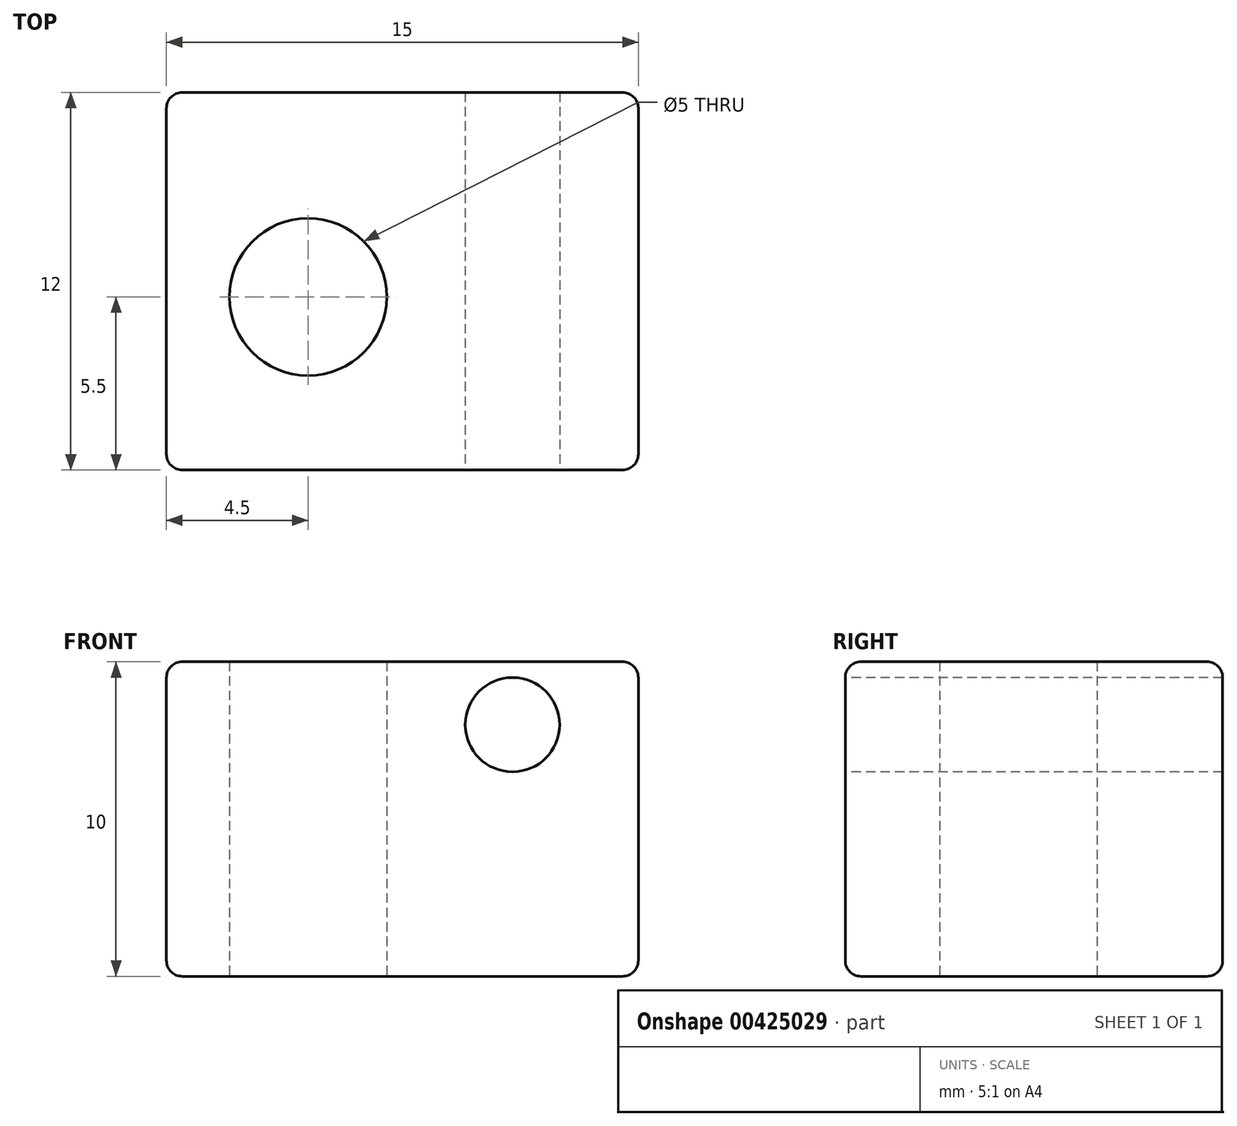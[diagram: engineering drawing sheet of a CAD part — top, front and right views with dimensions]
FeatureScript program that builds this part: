
annotation { "Feature Type Name" : "Feature", "Feature Type Description" : "" }
export const myFeature = defineFeature(function(context is Context, id is Id, definition is map)
    precondition{}
    {
        {
            var Q0;
            Q0=qCreatedBy(makeId("Top.planeOp"),FACE);
            var sketch = newSketch(context, id + "F0", { "sketchPlane" : qUnion([Q0])});
            skLineSegment(sketch, "E0.bottom", {"start": v(0, 0) * mm, "end": v(15, 0) * mm});
            skLineSegment(sketch, "E0.top", {"start": v(0, 12) * mm, "end": v(15, 12) * mm});
            skLineSegment(sketch, "E0.left", {"start": v(0, 0) * mm, "end": v(0, 12) * mm});
            skLineSegment(sketch, "E0.right", {"start": v(15, 0) * mm, "end": v(15, 12) * mm});
            skCircle(sketch, "E1", {"center": v(4.5, 5.5) * mm, "radius": 2.5 * mm});
            skSolve(sketch);
        }
        {
            var Q0;
            Q0=makeQuery(id+"F0.imprint","IMPRINT",FACE,{"disambiguationData":[TD([[makeQuery(id+"F0.imprint","IMPRINT",EDGE,{"derivedFrom":sQuery(id+"F0.wireOp",EDGE,"E0.bottom")}),1.0]])]});
            extrude(context, id + "F1", {"entities" : qUnion([Q0]), "endBound" : BoundingType.SYMMETRIC, "depth" : 10 * mm});
        }
        {
            var Q0;
            Q0=makeQuery(id+"F1.opExtrude","SWEPT_FACE",FACE,{"disambiguationData":[OSD([sQuery(id+"F0.wireOp",EDGE,"E0.bottom")])]});
            var sketch = newSketch(context, id + "F2", { "sketchPlane" : qUnion([Q0])});
            skCircle(sketch, "E2", {"center": v(11, 3) * mm, "radius": 1.5 * mm});
            skSolve(sketch);
        }
        {
            var Q0;
            Q0=makeQuery(id+"F2.imprint","IMPRINT",FACE,{"disambiguationData":[TD([[makeQuery(id+"F2.imprint","IMPRINT",EDGE,{"derivedFrom":sQuery(id+"F2.wireOp",EDGE,"E2")}),1.0]])]});
            extrude(context, id + "F3", {"entities" : qUnion([Q0]), "operationType" : NewBodyOperationType.REMOVE, "endBound" : BoundingType.THROUGH_ALL, "oppositeDirection" : true, "depth" : 25 * mm});
        }
        {
            var Q0;
            Q0=makeQuery(id+"F1.opExtrude","CAP_EDGE",EDGE,{"disambiguationData":[OSD([sQuery(id+"F0.wireOp",EDGE,"E0.bottom")])],"isStart":false});
            var Q1;
            Q1=makeQuery(id+"F1.opExtrude","CAP_EDGE",EDGE,{"disambiguationData":[OSD([sQuery(id+"F0.wireOp",EDGE,"E0.right")])],"isStart":false});
            var Q2;
            Q2=makeQuery(id+"F1.opExtrude","CAP_EDGE",EDGE,{"disambiguationData":[OSD([sQuery(id+"F0.wireOp",EDGE,"E0.top")])],"isStart":false});
            var Q3;
            Q3=makeQuery(id+"F1.opExtrude","CAP_EDGE",EDGE,{"disambiguationData":[OSD([sQuery(id+"F0.wireOp",EDGE,"E0.left")])],"isStart":false});
            fillet(context, id + "F4", {"entities" : qUnion([Q0, Q1, Q2, Q3]), "radius" : .5 * mm, "tangentPropagation" : true, "allowEdgeOverflow" : false});
        }
        {
            var Q0;
            Q0=makeQuery(id+"F1.opExtrude","SWEPT_EDGE",EDGE,{"disambiguationData":[OSD([sQuery(id+"F0.wireOp",EDGE,"E0.bottom"),sQuery(id+"F0.wireOp",EDGE,"E0.right")])]});
            var Q1;
            Q1=makeQuery(id+"F1.opExtrude","SWEPT_EDGE",EDGE,{"disambiguationData":[OSD([sQuery(id+"F0.wireOp",EDGE,"E0.bottom"),sQuery(id+"F0.wireOp",EDGE,"E0.left")])]});
            var Q2;
            Q2=makeQuery(id+"F1.opExtrude","SWEPT_EDGE",EDGE,{"disambiguationData":[OSD([sQuery(id+"F0.wireOp",EDGE,"E0.top"),sQuery(id+"F0.wireOp",EDGE,"E0.left")])]});
            var Q3;
            Q3=makeQuery(id+"F1.opExtrude","SWEPT_EDGE",EDGE,{"disambiguationData":[OSD([sQuery(id+"F0.wireOp",EDGE,"E0.top"),sQuery(id+"F0.wireOp",EDGE,"E0.right")])]});
            var Q4;
            Q4=makeQuery(id+"F1.opExtrude","CAP_EDGE",EDGE,{"disambiguationData":[OSD([sQuery(id+"F0.wireOp",EDGE,"E0.left")])],"isStart":true});
            var Q5;
            Q5=makeQuery(id+"F1.opExtrude","CAP_EDGE",EDGE,{"disambiguationData":[OSD([sQuery(id+"F0.wireOp",EDGE,"E0.top")])],"isStart":true});
            var Q6;
            Q6=makeQuery(id+"F1.opExtrude","CAP_EDGE",EDGE,{"disambiguationData":[OSD([sQuery(id+"F0.wireOp",EDGE,"E0.bottom")])],"isStart":true});
            var Q7;
            Q7=makeQuery(id+"F1.opExtrude","CAP_EDGE",EDGE,{"disambiguationData":[OSD([sQuery(id+"F0.wireOp",EDGE,"E0.right")])],"isStart":true});
            fillet(context, id + "F5", {"entities" : qUnion([Q0, Q1, Q2, Q3, Q4, Q5, Q6, Q7]), "radius" : .5 * mm, "tangentPropagation" : true, "allowEdgeOverflow" : false});
        }
    });
